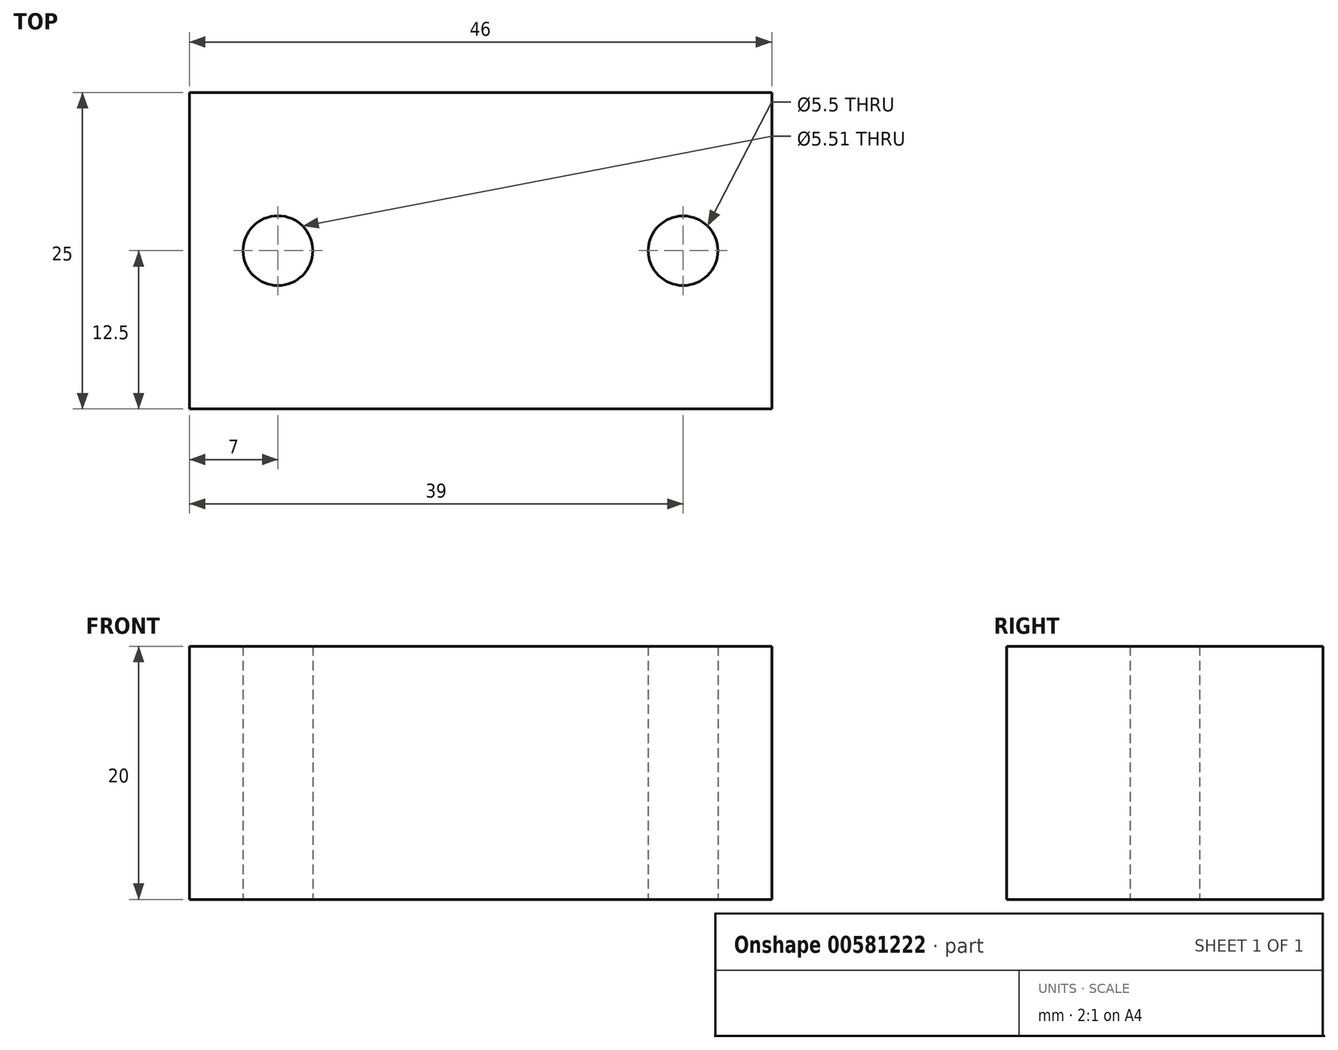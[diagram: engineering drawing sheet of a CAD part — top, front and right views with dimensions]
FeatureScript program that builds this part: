
annotation { "Feature Type Name" : "Feature", "Feature Type Description" : "" }
export const myFeature = defineFeature(function(context is Context, id is Id, definition is map)
    precondition{}
    {
        {
            var Q0;
            Q0=qCreatedBy(makeId("Top.planeOp"),FACE);
            var sketch = newSketch(context, id + "F0", { "sketchPlane" : qUnion([Q0])});
            skLineSegment(sketch, "E0.bottom", {"start": v(23, 12.5) * mm, "end": v(-23, 12.5) * mm});
            skLineSegment(sketch, "E0.top", {"start": v(23, -12.5) * mm, "end": v(-23, -12.5) * mm});
            skLineSegment(sketch, "E0.left", {"start": v(23, 12.5) * mm, "end": v(23, -12.5) * mm});
            skLineSegment(sketch, "E0.right", {"start": v(-23, 12.5) * mm, "end": v(-23, -12.5) * mm});
            skPoint(sketch, "E0.middle", {"position": v(0, 0) * mm});
            skCircle(sketch, "E1", {"center": v(16, 0) * mm, "radius": 2.75 * mm});
            skCircle(sketch, "E2.MirrorC", {"center": v(-16, 0) * mm, "radius": 2.76 * mm});
            skSolve(sketch);
        }
        {
            var Q0;
            Q0=qSketchRegion(id+"F0",true);
            extrude(context, id + "F1", {"entities" : qUnion([Q0]), "depth" : 20 * mm, "offsetDistance" : 25.4 * mm});
        }
    });
